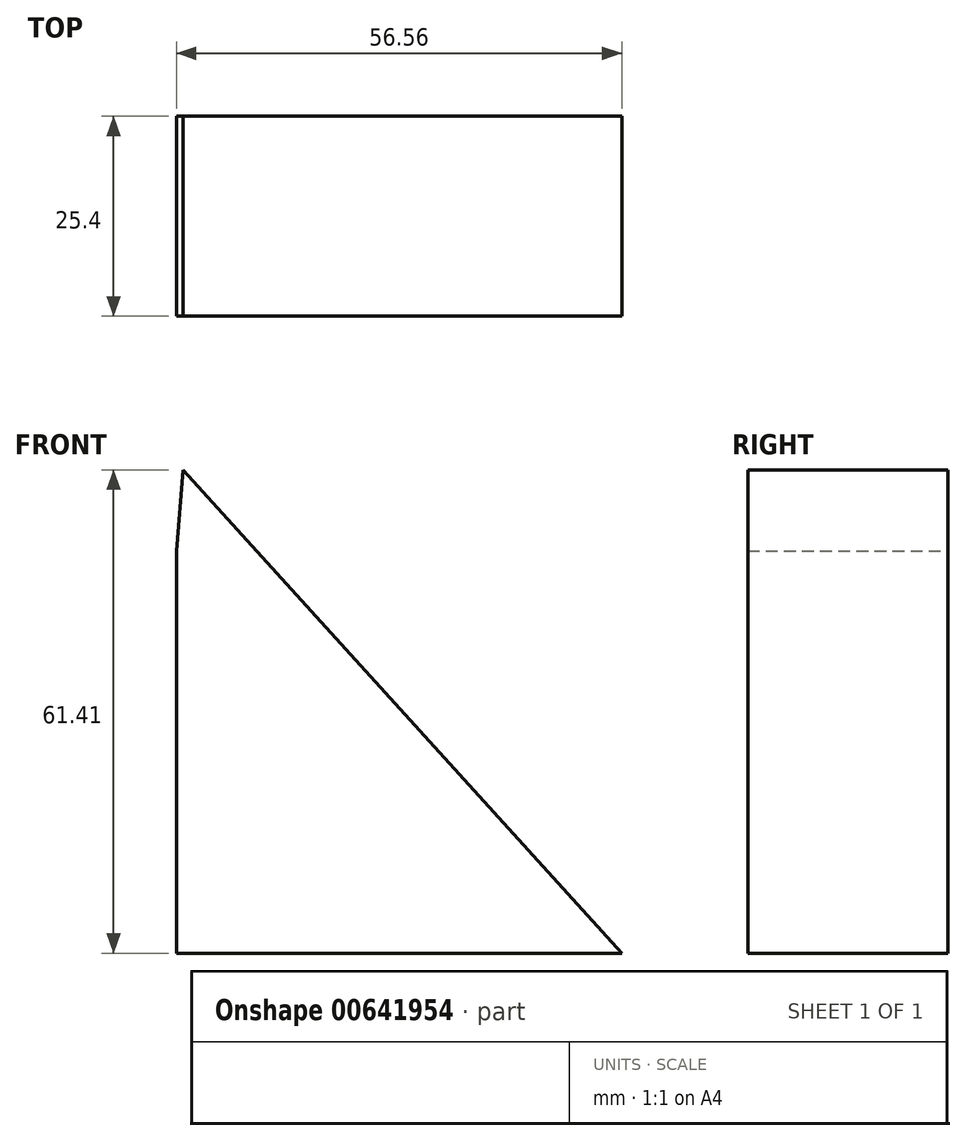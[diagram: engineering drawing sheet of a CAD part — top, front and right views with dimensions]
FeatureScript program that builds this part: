
annotation { "Feature Type Name" : "Feature", "Feature Type Description" : "" }
export const myFeature = defineFeature(function(context is Context, id is Id, definition is map)
    precondition{}
    {
        {
            var Q0;
            Q0=qCreatedBy(makeId("Front.planeOp"),FACE);
            var sketch = newSketch(context, id + "F0", { "sketchPlane" : qUnion([Q0])});
            skLineSegment(sketch, "E0", {"start": v(0, 0) * mm, "end": v(-55.7, 61.4) * mm});
            skLineSegment(sketch, "E1", {"start": v(-55.7, 61.4) * mm, "end": v(-55.7, 61.4) * mm});
            skLineSegment(sketch, "E2", {"start": v(-56.56, 51.12) * mm, "end": v(-56.56, 0) * mm});
            skLineSegment(sketch, "E3", {"start": v(-56.56, 0) * mm, "end": v(0, 0) * mm});
            skLineSegment(sketch, "E4", {"start": v(-55.7, 61.4) * mm, "end": v(-56.56, 51.12) * mm});
            skSolve(sketch);
        }
        {
            var Q0;
            Q0=makeQuery(id+"F0.imprint","IMPRINT",FACE,{"disambiguationData":[TD([[makeQuery(id+"F0.imprint","IMPRINT",EDGE,{"derivedFrom":sQuery(id+"F0.wireOp",EDGE,"E0")}),1.0]])]});
            extrude(context, id + "F1", {"entities" : qUnion([Q0]), "depth" : 25.4 * mm, "offsetDistance" : 25.4 * mm});
        }
    });
